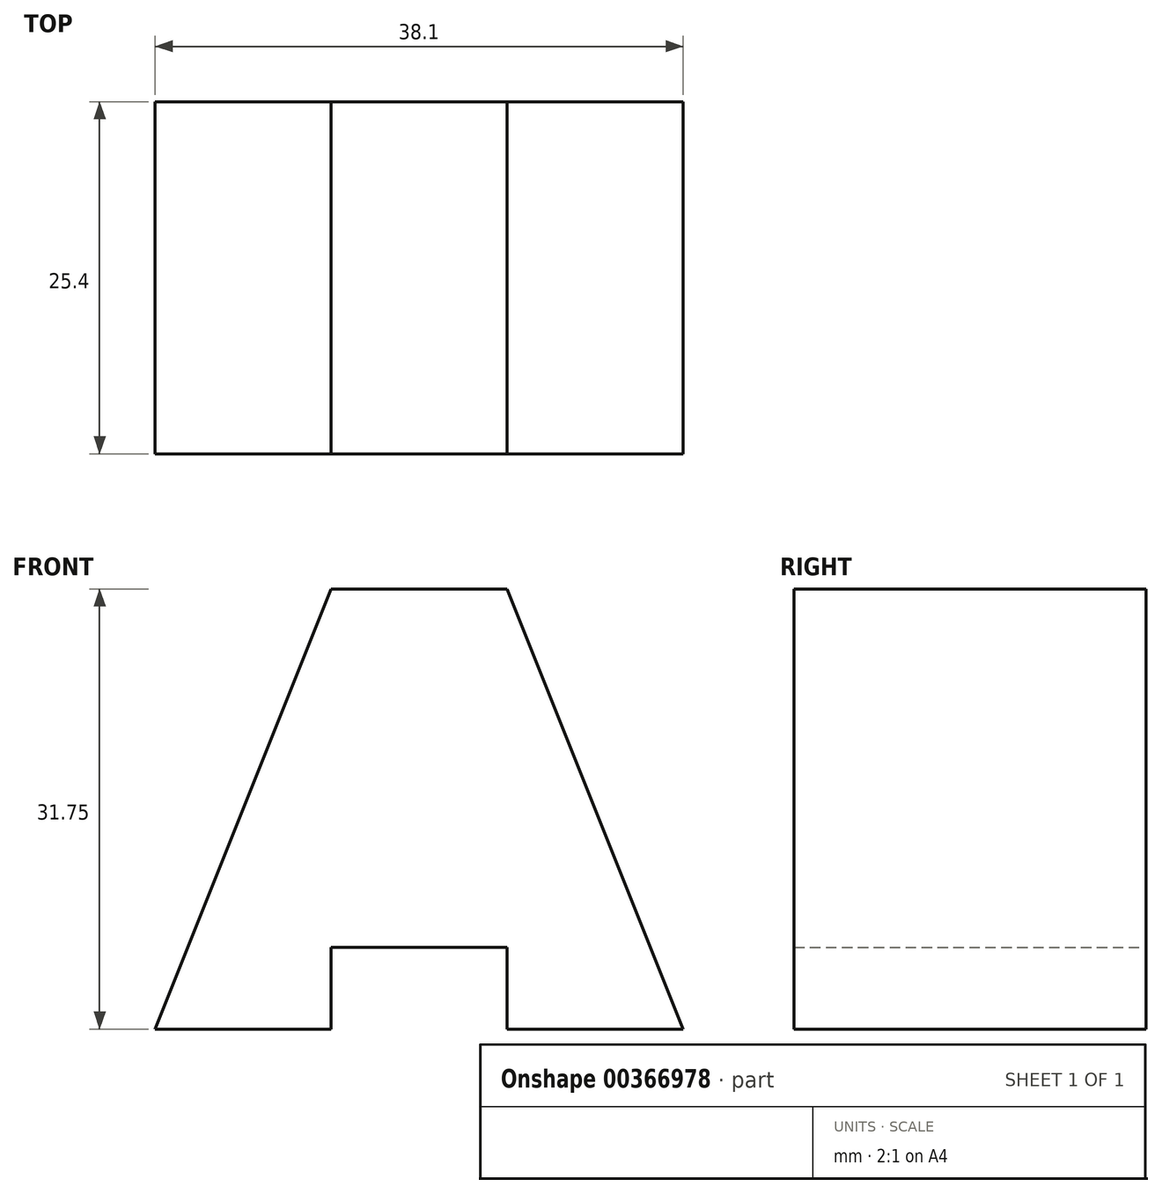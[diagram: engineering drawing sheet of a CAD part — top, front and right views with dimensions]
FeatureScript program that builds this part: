
annotation { "Feature Type Name" : "Feature", "Feature Type Description" : "" }
export const myFeature = defineFeature(function(context is Context, id is Id, definition is map)
    precondition{}
    {
        {
            var Q0;
            Q0=qCreatedBy(makeId("Front.planeOp"),FACE);
            var sketch = newSketch(context, id + "F0", { "sketchPlane" : qUnion([Q0])});
            skLineSegment(sketch, "E0", {"start": v(0, 0) * mm, "end": v(12.7, 0) * mm});
            skLineSegment(sketch, "E1", {"start": v(12.7, 0) * mm, "end": v(12.7, 5.9) * mm});
            skLineSegment(sketch, "E2", {"start": v(12.7, 5.9) * mm, "end": v(25.4, 5.9) * mm});
            skLineSegment(sketch, "E3", {"start": v(25.4, 5.9) * mm, "end": v(25.4, 0) * mm});
            skLineSegment(sketch, "E4", {"start": v(25.4, 0) * mm, "end": v(38.1, 0) * mm});
            skLineSegment(sketch, "E5", {"start": v(38.1, 0) * mm, "end": v(38.1, 31.75) * mm});
            skLineSegment(sketch, "E6", {"start": v(38.1, 31.75) * mm, "end": v(0, 31.75) * mm});
            skLineSegment(sketch, "E7", {"start": v(0, 31.75) * mm, "end": v(0, 0) * mm});
            skSolve(sketch);
        }
        {
            var Q0;
            Q0 = qSketchRegion(id + "F0", true);
            extrude(context, id + "F1", {"entities" : qUnion([Q0]), "depth" : 25.4 * mm});
        }
        {
            var Q0;
            Q0=makeQuery(id+"F1.opExtrude","CAP_FACE",FACE,{"disambiguationData":[OSD([sQuery(id+"F0.wireOp",EDGE,"E0"),sQuery(id+"F0.wireOp",EDGE,"E1"),sQuery(id+"F0.wireOp",EDGE,"E2"),sQuery(id+"F0.wireOp",EDGE,"E3"),sQuery(id+"F0.wireOp",EDGE,"E4"),sQuery(id+"F0.wireOp",EDGE,"E5"),sQuery(id+"F0.wireOp",EDGE,"E6"),sQuery(id+"F0.wireOp",EDGE,"E7")])],"isStart":false});
            var sketch = newSketch(context, id + "F2", { "sketchPlane" : qUnion([Q0])});
            skLineSegment(sketch, "E8", {"start": v(0, 0) * mm, "end": v(12.7, 31.75) * mm});
            skLineSegment(sketch, "E9", {"start": v(12.7, 31.75) * mm, "end": v(25.4, 31.75) * mm});
            skLineSegment(sketch, "E10", {"start": v(25.4, 31.75) * mm, "end": v(38.1, 0) * mm});
            skSolve(sketch);
        }
        {
            var Q0;
            {var subQ0=sQuery(id+"F2.wireOp",EDGE,"E8");Q0=makeQuery(id+"F2.imprint","IMPRINT",FACE,{"disambiguationData":[TD([[makeQuery(id+"F2.imprint","IMPRINT",EDGE,{"derivedFrom":subQ0}),1.0]])]});}
            extrude(context, id + "F3", {"entities" : qUnion([Q0]), "operationType" : NewBodyOperationType.REMOVE, "oppositeDirection" : true, "depth" : 25.4 * mm});
        }
        {
            var Q0;
            Q0=makeQuery(id+"F1.opExtrude","CAP_FACE",FACE,{"disambiguationData":[OSD([sQuery(id+"F0.wireOp",EDGE,"E0"),sQuery(id+"F0.wireOp",EDGE,"E1"),sQuery(id+"F0.wireOp",EDGE,"E2"),sQuery(id+"F0.wireOp",EDGE,"E3"),sQuery(id+"F0.wireOp",EDGE,"E4"),sQuery(id+"F0.wireOp",EDGE,"E5"),sQuery(id+"F0.wireOp",EDGE,"E6"),sQuery(id+"F0.wireOp",EDGE,"E7")])],"isStart":false});
            var sketch = newSketch(context, id + "F4", { "sketchPlane" : qUnion([Q0])});
            skLineSegment(sketch, "E11", {"start": v(38.1, 0) * mm, "end": v(25.4, 31.75) * mm});
            skSolve(sketch);
        }
        {
            var Q0;
            {var subQ0=sQuery(id+"F4.wireOp",EDGE,"E11");Q0=makeQuery(id+"F4.imprint","IMPRINT",FACE,{"disambiguationData":[TD([[makeQuery(id+"F4.imprint","IMPRINT",EDGE,{"derivedFrom":subQ0}),-1.0]])]});}
            extrude(context, id + "F5", {"entities" : qUnion([Q0]), "operationType" : NewBodyOperationType.REMOVE, "oppositeDirection" : true, "depth" : 25.4 * mm});
        }
    });
